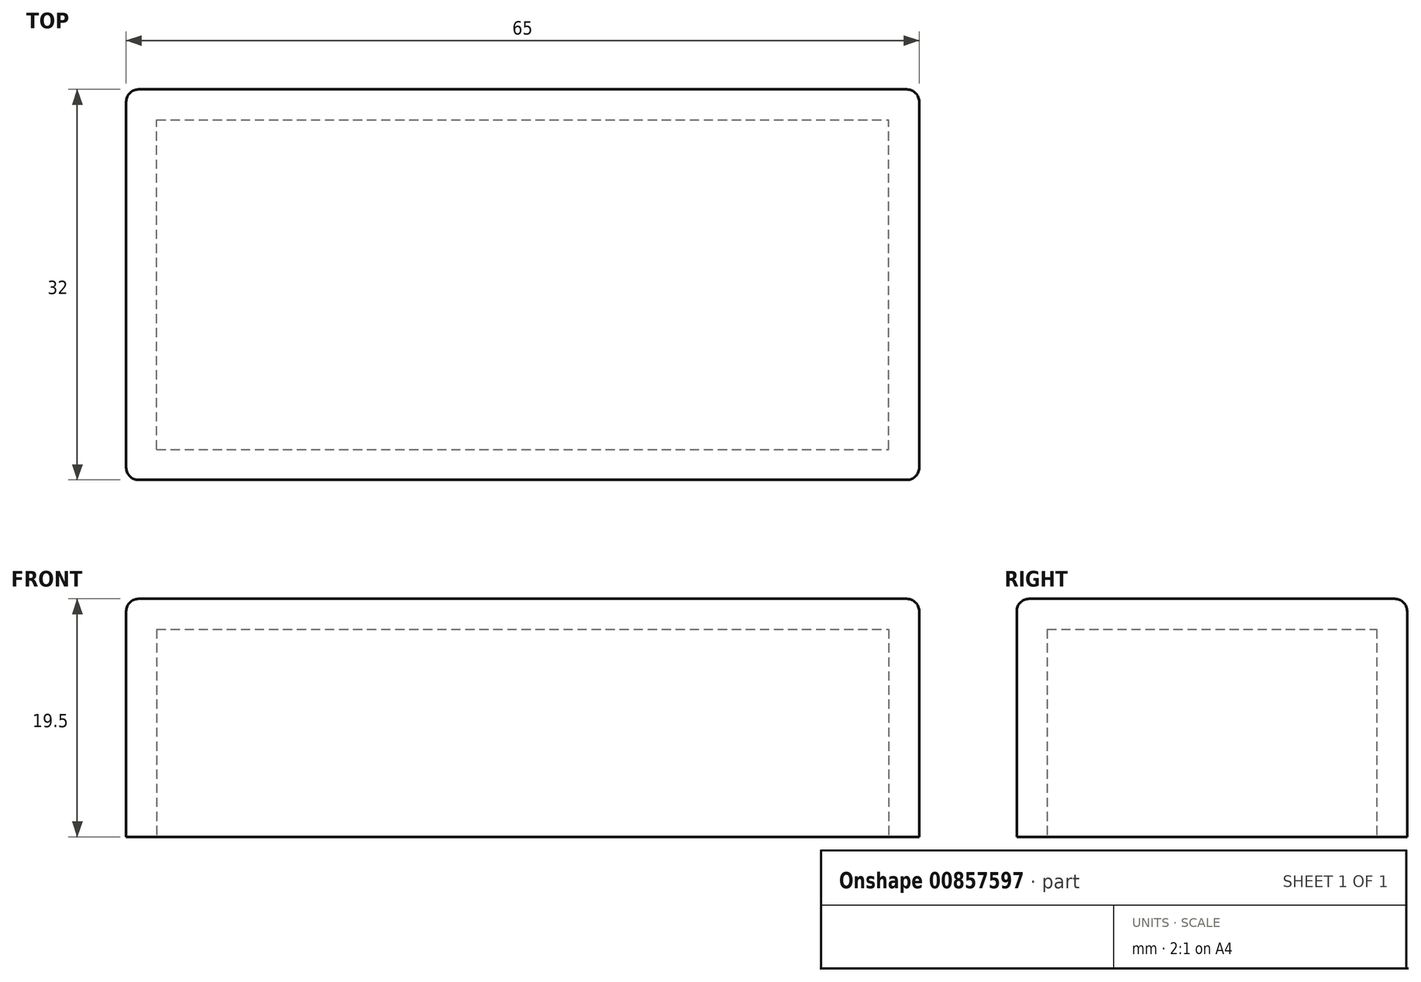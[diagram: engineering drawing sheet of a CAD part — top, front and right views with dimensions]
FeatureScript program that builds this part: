
annotation { "Feature Type Name" : "Feature", "Feature Type Description" : "" }
export const myFeature = defineFeature(function(context is Context, id is Id, definition is map)
    precondition{}
    {
        {
            var Q0;
            Q0=qCreatedBy(makeId("Top.planeOp"),FACE);
            var sketch = newSketch(context, id + "F0", { "sketchPlane" : qUnion([Q0])});
            skLineSegment(sketch, "E0.bottom", {"start": v(0, 0) * mm, "end": v(60, 0) * mm});
            skLineSegment(sketch, "E0.top", {"start": v(0, 27) * mm, "end": v(60, 27) * mm});
            skLineSegment(sketch, "E0.left", {"start": v(0, 0) * mm, "end": v(0, 27) * mm});
            skLineSegment(sketch, "E0.right", {"start": v(60, 0) * mm, "end": v(60, 27) * mm});
            skLineSegment(sketch, "E1.bottom", {"start": v(-2.5, 29.5) * mm, "end": v(62.5, 29.5) * mm});
            skLineSegment(sketch, "E1.top", {"start": v(-2.5, 0) * mm, "end": v(62.5, 0) * mm});
            skLineSegment(sketch, "E1.left", {"start": v(-2.5, 29.5) * mm, "end": v(-2.5, 0) * mm});
            skLineSegment(sketch, "E1.right", {"start": v(62.5, 29.5) * mm, "end": v(62.5, 0) * mm});
            skLineSegment(sketch, "E2.top", {"start": v(-2.5, -2.5) * mm, "end": v(62.5, -2.5) * mm});
            skLineSegment(sketch, "E2.left", {"start": v(-2.5, 0) * mm, "end": v(-2.5, -2.5) * mm});
            skLineSegment(sketch, "E2.right", {"start": v(62.5, 0) * mm, "end": v(62.5, -2.5) * mm});
            skSolve(sketch);
        }
        {
            var Q0;
            Q0=makeQuery(id+"F0.imprint","IMPRINT",FACE,{"disambiguationData":[TD([[makeQuery(id+"F0.imprint","IMPRINT",EDGE,{"derivedFrom":sQuery(id+"F0.wireOp",EDGE,"E0.bottom")}),-1.0]])]});
            var Q1;
            Q1=makeQuery(id+"F0.imprint","IMPRINT",FACE,{"disambiguationData":[TD([[makeQuery(id+"F0.imprint","IMPRINT",EDGE,{"derivedFrom":sQuery(id+"F0.wireOp",EDGE,"E0.top")}),1.0]])]});
            extrude(context, id + "F1", {"entities" : qUnion([Q0, Q1]), "flatOperationType" : FlatOperationType.REMOVE, "depth" : 17 * mm, "offsetDistance" : 25 * mm, "domain" : OperationDomain.MODEL});
        }
        {
            var Q0;
            Q0=makeQuery(id+"F1.opExtrude","CAP_FACE",FACE,{"disambiguationData":[OSD([sQuery(id+"F0.wireOp",EDGE,"E0.bottom"),sQuery(id+"F0.wireOp",EDGE,"E0.top"),sQuery(id+"F0.wireOp",EDGE,"E0.left"),sQuery(id+"F0.wireOp",EDGE,"E0.right"),sQuery(id+"F0.wireOp",EDGE,"E1.bottom"),sQuery(id+"F0.wireOp",EDGE,"E1.top"),sQuery(id+"F0.wireOp",EDGE,"E1.left"),sQuery(id+"F0.wireOp",EDGE,"E1.right")])],"isStart":false});
            var sketch = newSketch(context, id + "F2", { "sketchPlane" : qUnion([Q0])});
            skLineSegment(sketch, "E3", {"start": v(0, 27) * mm, "end": v(60, 27) * mm});
            skLineSegment(sketch, "E4", {"start": v(0, 0) * mm, "end": v(60, 0) * mm});
            skSolve(sketch);
        }
        {
            var Q0;
            Q0=makeQuery(id+"F0.imprint","IMPRINT",FACE,{"disambiguationData":[TD([[makeQuery(id+"F0.imprint","IMPRINT",EDGE,{"derivedFrom":sQuery(id+"F0.wireOp",EDGE,"E2.top")}),1.0]])]});
            extrude(context, id + "F3", {"entities" : qUnion([Q0]), "operationType" : NewBodyOperationType.ADD, "flatOperationType" : FlatOperationType.REMOVE, "depth" : 17 * mm, "offsetDistance" : 25 * mm, "domain" : OperationDomain.MODEL});
        }
        {
            var Q0;
            Q0=makeQuery(id+"F1.opExtrude","CAP_FACE",FACE,{"disambiguationData":[OSD([sQuery(id+"F0.wireOp",EDGE,"E0.top"),sQuery(id+"F0.wireOp",EDGE,"E0.left"),sQuery(id+"F0.wireOp",EDGE,"E0.right"),sQuery(id+"F0.wireOp",EDGE,"E1.bottom"),sQuery(id+"F0.wireOp",EDGE,"E1.left"),sQuery(id+"F0.wireOp",EDGE,"E1.right"),sQuery(id+"F0.wireOp",EDGE,"E1.top")])],"isStart":false});
            var sketch = newSketch(context, id + "F4", { "sketchPlane" : qUnion([Q0])});
            skLineSegment(sketch, "E5", {"start": v(0, 0) * mm, "end": v(60, 0) * mm});
            skSolve(sketch);
        }
        {
            var Q0;
            Q0=makeQuery(id+"F2.imprint","IMPRINT",FACE,{"disambiguationData":[TD([[makeQuery(id+"F2.imprint","IMPRINT",EDGE,{"derivedFrom":sQuery(id+"F2.wireOp",EDGE,"E3")}),-1.0]])]});
            var Q1;
            Q1=makeQuery(id+"F4.imprint","IMPRINT",FACE,{"disambiguationData":[TD([[makeQuery(id+"F4.imprint","IMPRINT",EDGE,{"derivedFrom":sQuery(id+"F4.wireOp",EDGE,"E5")}),-1.0]])]});
            extrude(context, id + "F5", {"entities" : qUnion([Q0, Q1]), "operationType" : NewBodyOperationType.ADD, "depth" : 2.5 * mm, "offsetDistance" : 25 * mm});
        }
        {
            var Q0;
            Q0=makeQuery(id+"F5.opExtrude","CAP_EDGE",EDGE,{"disambiguationData":[OSD([sQuery(id+"F0.wireOp",EDGE,"E1.bottom")])],"isStart":false});
            var Q1;
            Q1=makeQuery(id+"F5.opExtrude","CAP_EDGE",EDGE,{"disambiguationData":[OSD([sQuery(id+"F0.wireOp",EDGE,"E1.left"),sQuery(id+"F0.wireOp",EDGE,"E2.left")])],"isStart":false});
            var Q2;
            Q2=makeQuery(id+"F5.opExtrude","CAP_EDGE",EDGE,{"disambiguationData":[OSD([sQuery(id+"F0.wireOp",EDGE,"E1.right"),sQuery(id+"F0.wireOp",EDGE,"E2.right")])],"isStart":false});
            var Q3;
            Q3=makeQuery(id+"F5.opExtrude","CAP_EDGE",EDGE,{"disambiguationData":[OSD([sQuery(id+"F0.wireOp",EDGE,"E2.top")])],"isStart":false});
            var Q4;
            {var subQ0=sQuery(id+"F0.wireOp",EDGE,"E1.left");var subQ1=sQuery(id+"F0.wireOp",EDGE,"E1.bottom");Q4=makeQuery(id+"F5.boolean.opBoolean","MERGE",EDGE,{"derivedFrom":[makeQuery(id+"F1.opExtrude","SWEPT_EDGE",EDGE,{"disambiguationData":[OSD([subQ1,subQ0])]}),makeQuery(id+"F5.opExtrude","SWEPT_EDGE",EDGE,{"disambiguationData":[OSD([subQ1,subQ0,sQuery(id+"F0.wireOp",EDGE,"E2.left")])]})]});}
            var Q5;
            {var subQ0=sQuery(id+"F0.wireOp",EDGE,"E1.right");var subQ1=sQuery(id+"F0.wireOp",EDGE,"E1.bottom");Q5=makeQuery(id+"F5.boolean.opBoolean","MERGE",EDGE,{"derivedFrom":[makeQuery(id+"F1.opExtrude","SWEPT_EDGE",EDGE,{"disambiguationData":[OSD([subQ1,subQ0])]}),makeQuery(id+"F5.opExtrude","SWEPT_EDGE",EDGE,{"disambiguationData":[OSD([subQ1,subQ0,sQuery(id+"F0.wireOp",EDGE,"E2.right")])]})]});}
            var Q6;
            {var subQ0=sQuery(id+"F0.wireOp",EDGE,"E2.right");var subQ1=sQuery(id+"F0.wireOp",EDGE,"E2.top");Q6=makeQuery(id+"F5.boolean.opBoolean","MERGE",EDGE,{"derivedFrom":[makeQuery(id+"F3.opExtrude","SWEPT_EDGE",EDGE,{"disambiguationData":[OSD([subQ1,subQ0])]}),makeQuery(id+"F5.opExtrude","SWEPT_EDGE",EDGE,{"disambiguationData":[OSD([sQuery(id+"F0.wireOp",EDGE,"E1.right"),subQ1,subQ0])]})]});}
            var Q7;
            {var subQ0=sQuery(id+"F0.wireOp",EDGE,"E2.left");var subQ1=sQuery(id+"F0.wireOp",EDGE,"E2.top");Q7=makeQuery(id+"F5.boolean.opBoolean","MERGE",EDGE,{"derivedFrom":[makeQuery(id+"F3.opExtrude","SWEPT_EDGE",EDGE,{"disambiguationData":[OSD([subQ1,subQ0])]}),makeQuery(id+"F5.opExtrude","SWEPT_EDGE",EDGE,{"disambiguationData":[OSD([sQuery(id+"F0.wireOp",EDGE,"E1.left"),subQ1,subQ0])]})]});}
            fillet(context, id + "F6", {"entities" : qUnion([Q0, Q1, Q2, Q3, Q4, Q5, Q6, Q7]), "radius" : 1 * mm, "tangentPropagation" : true, "allowEdgeOverflow" : false});
        }
    });
